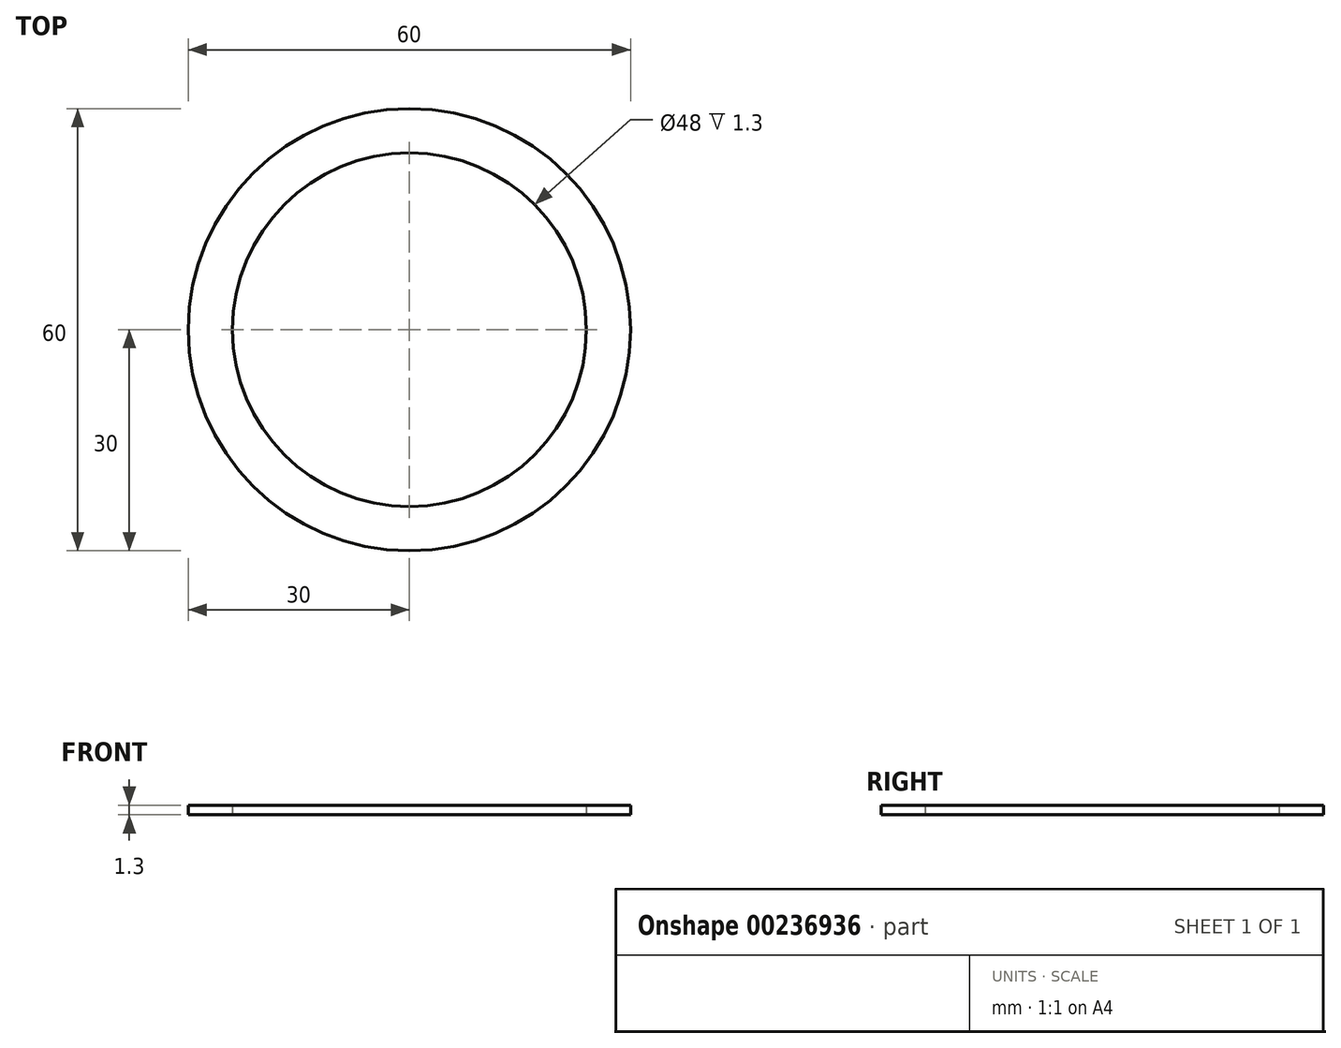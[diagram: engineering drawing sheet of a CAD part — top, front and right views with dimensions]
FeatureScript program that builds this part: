
annotation { "Feature Type Name" : "Feature", "Feature Type Description" : "" }
export const myFeature = defineFeature(function(context is Context, id is Id, definition is map)
    precondition{}
    {
        {
            var Q0;
            Q0=qCreatedBy(makeId("Top.planeOp"),FACE);
            var sketch = newSketch(context, id + "F0", { "sketchPlane" : qUnion([Q0])});
            skCircle(sketch, "E0", {"center": v(0, 0) * mm, "radius": 30 * mm});
            skCircle(sketch, "E1", {"center": v(0, 0) * mm, "radius": 24 * mm});
            skSolve(sketch);
        }
        {
            var Q0;
            Q0 = qSketchRegion(id + "F0", true);
            extrude(context, id + "F1", {"entities" : qUnion([Q0]), "depth" : 1.3 * mm});
        }
    });
